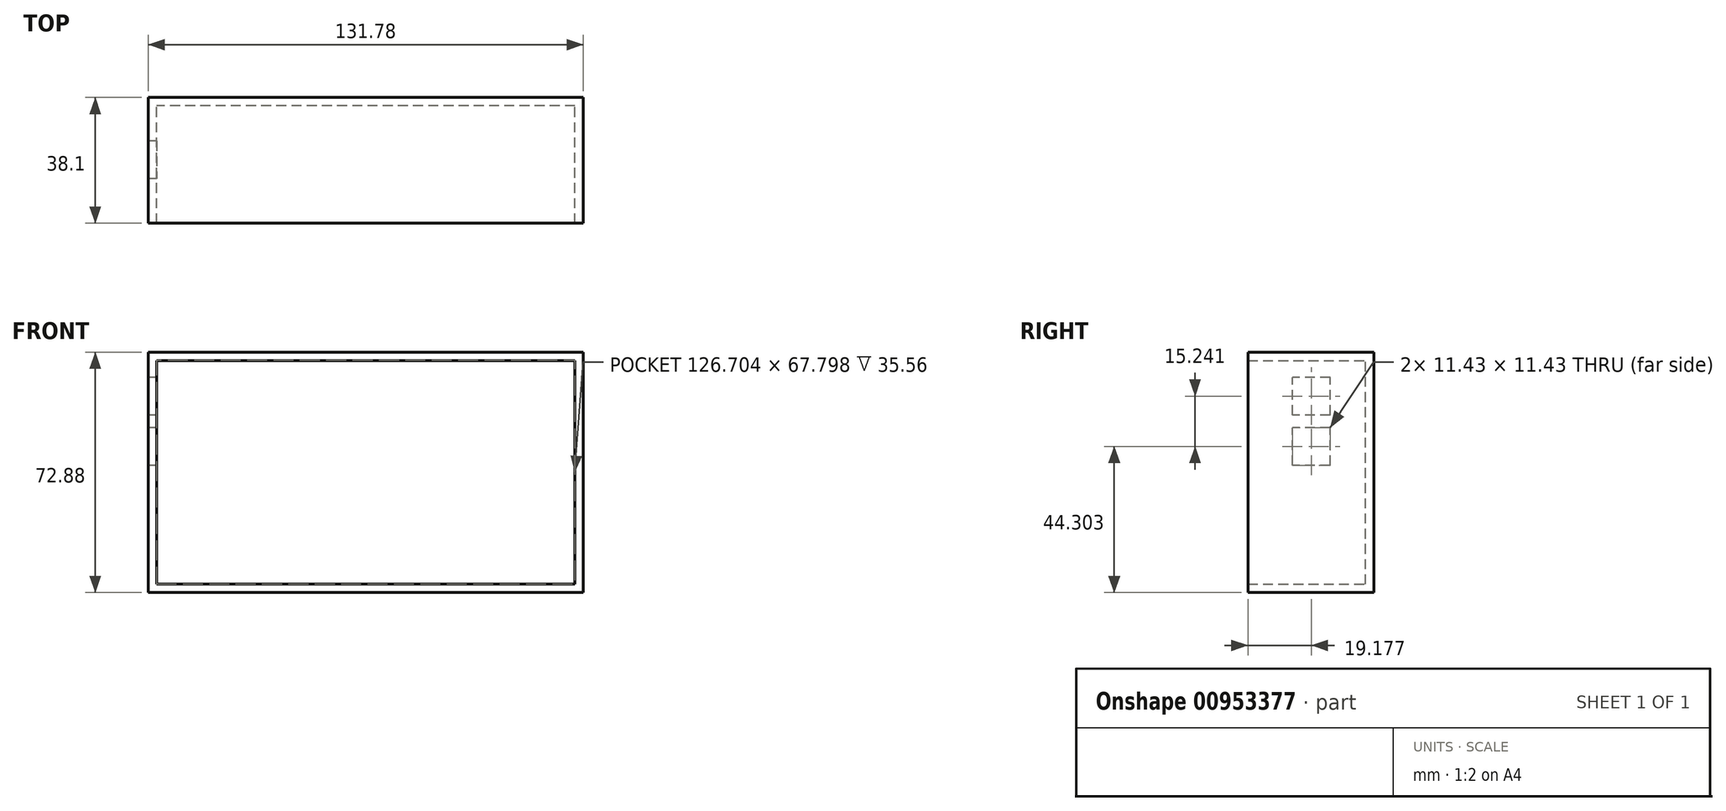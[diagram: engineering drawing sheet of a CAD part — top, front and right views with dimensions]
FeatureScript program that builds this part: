
annotation { "Feature Type Name" : "Feature", "Feature Type Description" : "" }
export const myFeature = defineFeature(function(context is Context, id is Id, definition is map)
    precondition{}
    {
        {
            var Q0;
            Q0=qCreatedBy(makeId("Front.planeOp"),FACE);
            var sketch = newSketch(context, id + "F0", { "sketchPlane" : qUnion([Q0])});
            skLineSegment(sketch, "E0.bottom", {"start": v(65.9, -36.44) * mm, "end": v(-65.9, -36.44) * mm});
            skLineSegment(sketch, "E0.top", {"start": v(65.9, 36.44) * mm, "end": v(-65.9, 36.44) * mm});
            skLineSegment(sketch, "E0.left", {"start": v(65.9, -36.44) * mm, "end": v(65.9, 36.44) * mm});
            skLineSegment(sketch, "E0.right", {"start": v(-65.9, -36.44) * mm, "end": v(-65.9, 36.44) * mm});
            skPoint(sketch, "E0.middle", {"position": v(0, 0) * mm});
            skSolve(sketch);
        }
        {
            var Q0;
            Q0=makeQuery(id+"F0.imprint","IMPRINT",FACE,{"disambiguationData":[TD([[makeQuery(id+"F0.imprint","IMPRINT",EDGE,{"derivedFrom":sQuery(id+"F0.wireOp",EDGE,"E0.bottom")}),-1.0]])]});
            extrude(context, id + "F1", {"entities" : qUnion([Q0]), "depth" : 38.1 * mm, "offsetDistance" : 25.4 * mm});
        }
        {
            var Q0;
            Q0=makeQuery(id+"F1.opExtrude","CAP_FACE",FACE,{"disambiguationData":[OSD([sQuery(id+"F0.wireOp",EDGE,"E0.bottom"),sQuery(id+"F0.wireOp",EDGE,"E0.top"),sQuery(id+"F0.wireOp",EDGE,"E0.left"),sQuery(id+"F0.wireOp",EDGE,"E0.right")])],"isStart":false});
            shell(context, id + "F2", {"entities" : qUnion([Q0]), "thickness" : 2.54 * mm});
        }
        {
            var Q0;
            Q0=makeQuery(id+"F1.opExtrude","SWEPT_FACE",FACE,{"disambiguationData":[OSD([sQuery(id+"F0.wireOp",EDGE,"E0.right")])]});
            var sketch = newSketch(context, id + "F3", { "sketchPlane" : qUnion([Q0])});
            skLineSegment(sketch, "E1.bottom", {"start": v(13.2, 17.39) * mm, "end": v(24.64, 17.39) * mm});
            skLineSegment(sketch, "E1.top", {"start": v(13.2, 28.82) * mm, "end": v(24.64, 28.82) * mm});
            skLineSegment(sketch, "E1.left", {"start": v(13.2, 17.39) * mm, "end": v(13.2, 28.82) * mm});
            skLineSegment(sketch, "E1.right", {"start": v(24.64, 17.39) * mm, "end": v(24.64, 28.82) * mm});
            skPoint(sketch, "E1.middle", {"position": v(18.92, 23.1) * mm});
            skLineSegment(sketch, "E2.bottom", {"start": v(13.2, 0) * mm, "end": v(22.07, 0) * mm});
            skLineSegment(sketch, "E2.top", {"start": v(13.2, 16.12) * mm, "end": v(22.07, 16.12) * mm});
            skLineSegment(sketch, "E2.left", {"start": v(13.2, 0) * mm, "end": v(13.2, 16.12) * mm});
            skLineSegment(sketch, "E2.right", {"start": v(22.07, 0) * mm, "end": v(22.07, 16.12) * mm});
            skPoint(sketch, "E2.middle", {"position": v(17.64, 8.06) * mm});
            skSolve(sketch);
        }
        {
            var Q0;
            Q0=makeQuery(id+"F3.imprint","IMPRINT",FACE,{"disambiguationData":[TD([[makeQuery(id+"F3.imprint","IMPRINT",EDGE,{"derivedFrom":sQuery(id+"F3.wireOp",EDGE,"E1.bottom")}),1.0]])]});
            extrude(context, id + "F4", {"entities" : qUnion([Q0]), "operationType" : NewBodyOperationType.REMOVE, "oppositeDirection" : true, "depth" : 25.4 * mm, "offsetDistance" : 25.4 * mm});
        }
        {
            var Q0;
            Q0=makeQuery(id+"F1.opExtrude","SWEPT_FACE",FACE,{"disambiguationData":[OSD([sQuery(id+"F0.wireOp",EDGE,"E0.right")])]});
            var sketch = newSketch(context, id + "F5", { "sketchPlane" : qUnion([Q0])});
            skLineSegment(sketch, "E3.bottom", {"start": v(13.2, 2.15) * mm, "end": v(24.64, 2.15) * mm});
            skLineSegment(sketch, "E3.top", {"start": v(13.2, 13.58) * mm, "end": v(24.64, 13.58) * mm});
            skLineSegment(sketch, "E3.left", {"start": v(13.2, 2.15) * mm, "end": v(13.2, 13.58) * mm});
            skLineSegment(sketch, "E3.right", {"start": v(24.64, 2.15) * mm, "end": v(24.64, 13.58) * mm});
            skPoint(sketch, "E3.middle", {"position": v(18.92, 7.86) * mm});
            skSolve(sketch);
        }
        {
            var Q0;
            Q0=makeQuery(id+"F5.imprint","IMPRINT",FACE,{"disambiguationData":[TD([[makeQuery(id+"F5.imprint","IMPRINT",EDGE,{"derivedFrom":sQuery(id+"F5.wireOp",EDGE,"E3.bottom")}),1.0]])]});
            extrude(context, id + "F6", {"entities" : qUnion([Q0]), "operationType" : NewBodyOperationType.REMOVE, "oppositeDirection" : true, "depth" : 25.4 * mm, "offsetDistance" : 25.4 * mm});
        }
    });
